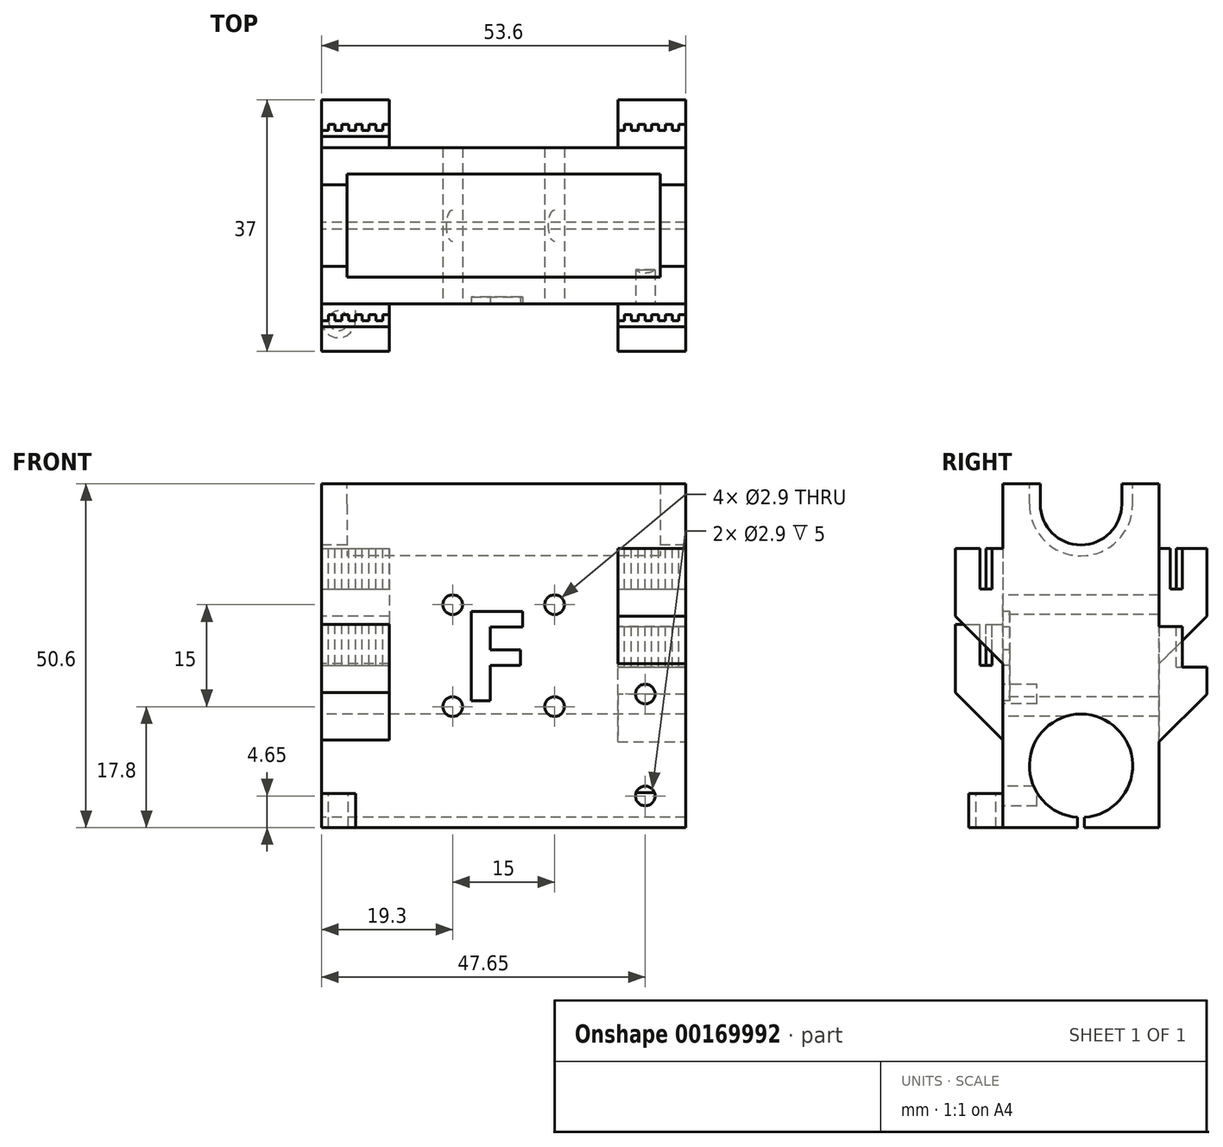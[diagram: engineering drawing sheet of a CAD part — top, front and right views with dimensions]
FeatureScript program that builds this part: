
annotation { "Feature Type Name" : "Feature", "Feature Type Description" : "" }
export const myFeature = defineFeature(function(context is Context, id is Id, definition is map)
    precondition{}
    {
        {
            assignVariable(context, id + "F0", {"name" : "LM8LUU", "anyValue" : 1.8});
        }
        {
            var Q0;
            Q0=qCreatedBy(makeId("Top.planeOp"),FACE);
            var sketch = newSketch(context, id + "F1", { "sketchPlane" : qUnion([Q0])});
            skLineSegment(sketch, "E0.bottom", {"start": v(0, 0) * mm, "end": v(53.6, 0) * mm});
            skLineSegment(sketch, "E0.top", {"start": v(0, 23) * mm, "end": v(53.6, 23) * mm});
            skLineSegment(sketch, "E0.left", {"start": v(0, 0) * mm, "end": v(0, 23) * mm});
            skLineSegment(sketch, "E0.right", {"start": v(53.6, 0) * mm, "end": v(53.6, 23) * mm});
            skSolve(sketch);
        }
        {
            var Q0;
            Q0=qSketchRegion(id+"F1",true);
            extrude(context, id + "F2", {"entities" : qUnion([Q0]), "depth" : 50.6 * mm});
        }
        {
            var Q0;
            Q0=makeQuery(id+"F2.opExtrude","SWEPT_FACE",FACE,{"disambiguationData":[OSD([sQuery(id+"F1.wireOp",EDGE,"E0.left")])]});
            var sketch = newSketch(context, id + "F3", { "sketchPlane" : qUnion([Q0])});
            skCircle(sketch, "E1", {"center": v(-11.5, 9.1) * mm, "radius": 7.6 * mm});
            skCircle(sketch, "E2", {"center": v(-11.5, 47.6) * mm, "radius": 6 * mm});
            skLineSegment(sketch, "E3", {"start": v(-23, 47.6) * mm, "end": v(0, 47.6) * mm, "construction": true});
            skLineSegment(sketch, "E4", {"start": v(-17.5, 50.6) * mm, "end": v(-17.5, 47.6) * mm});
            skLineSegment(sketch, "E5", {"start": v(-5.5, 50.6) * mm, "end": v(-5.5, 47.6) * mm});
            skLineSegment(sketch, "E6", {"start": v(-23, 9.1) * mm, "end": v(0, 9.1) * mm, "construction": true});
            skLineSegment(sketch, "E7", {"start": v(-11.5, 9.1) * mm, "end": v(-11.5, 0) * mm, "construction": true});
            skLineSegment(sketch, "E8", {"start": v(-11.5, 0) * mm, "end": v(-12, 0) * mm});
            skLineSegment(sketch, "E9", {"start": v(-12, 0) * mm, "end": v(-12, 1.52) * mm});
            skLineSegment(sketch, "E10", {"start": v(-12, 1.52) * mm, "end": v(-11, 1.52) * mm});
            skLineSegment(sketch, "E11", {"start": v(-11, 1.52) * mm, "end": v(-11, 0) * mm});
            skLineSegment(sketch, "E12", {"start": v(-11, 0) * mm, "end": v(-11.5, 0) * mm});
            skCircle(sketch, "E13", {"center": v(-11.5, 47.6) * mm, "radius": 7.6 * mm});
            skLineSegment(sketch, "E14", {"start": v(-3.9, 47.6) * mm, "end": v(-3.9, 50.6) * mm});
            skLineSegment(sketch, "E15", {"start": v(-19.1, 47.6) * mm, "end": v(-19.1, 50.6) * mm});
            skSolve(sketch);
        }
        {
            var Q0;
            {var subQ0=sQuery(id+"F3.wireOp",EDGE,"61a55092-bd36-442a-954f-b1d305e603b2");var subQ1=sQuery(id+"F3.wireOp",EDGE,"E1");var subQ3=makeQuery(id+"F3.imprint","INTERSECT",VERTEX,{"disambiguationData":[OD(0.0)],"derivedFrom":[subQ1,subQ0]});Q0=makeQuery(id+"F3.imprint","IMPRINT",FACE,{"disambiguationData":[TD([[makeQuery(id+"F3.imprint","IMPRINT",EDGE,{"disambiguationData":[TD([[subQ3,-1.0]])],"derivedFrom":subQ1}),1.0]])]});}
            var Q1;
            {var subQ0=sQuery(id+"F3.wireOp",EDGE,"ccdeb851-c584-4ba8-b480-4501c20c5f95");var subQ1=sQuery(id+"F3.wireOp",EDGE,"E1");var subQ3=makeQuery(id+"F3.imprint","INTERSECT",VERTEX,{"disambiguationData":[OD(0.0)],"derivedFrom":[subQ1,subQ0]});Q1=makeQuery(id+"F3.imprint","IMPRINT",FACE,{"disambiguationData":[TD([[makeQuery(id+"F3.imprint","IMPRINT",EDGE,{"disambiguationData":[TD([[subQ3,1.0]])],"derivedFrom":subQ1}),1.0]])]});}
            var Q2;
            Q2=makeQuery(id+"F3.imprint","IMPRINT",FACE,{"disambiguationData":[TD([[makeQuery(id+"F3.imprint","IMPRINT",EDGE,{"derivedFrom":sQuery(id+"F3.wireOp",EDGE,"E8")}),-1.0]])]});
            var Q3;
            {var subQ0=sQuery(id+"F3.wireOp",EDGE,"E10");Q3=makeQuery(id+"F3.imprint","IMPRINT",FACE,{"disambiguationData":[TD([[makeQuery(id+"F3.imprint","IMPRINT",EDGE,{"derivedFrom":subQ0}),-1.0]])]});}
            var Q4;
            {var subQ3=sQuery(id+"F3.wireOp",EDGE,"84843404-b723-4df1-a710-1511c094684b");Q4=makeQuery(id+"F3.imprint","IMPRINT",FACE,{"disambiguationData":[TD([[makeQuery(id+"F3.imprint","IMPRINT",EDGE,{"derivedFrom":subQ3}),-1.0]])]});}
            var Q5;
            {var subQ3=sQuery(id+"F3.wireOp",EDGE,"84843404-b723-4df1-a710-1511c094684b");Q5=makeQuery(id+"F3.imprint","IMPRINT",FACE,{"disambiguationData":[TD([[makeQuery(id+"F3.imprint","IMPRINT",EDGE,{"derivedFrom":subQ3}),1.0]])]});}
            var Q6;
            {var subQ7=sQuery(id+"F3.wireOp",EDGE,"E10");Q6=makeQuery(id+"F3.imprint","IMPRINT",FACE,{"disambiguationData":[TD([[makeQuery(id+"F3.imprint","IMPRINT",EDGE,{"derivedFrom":subQ7}),1.0]])]});}
            var Q7;
            {var subQ3=sQuery(id+"F3.wireOp",EDGE,"E5");Q7=makeQuery(id+"F3.imprint","IMPRINT",FACE,{"disambiguationData":[TD([[makeQuery(id+"F3.imprint","IMPRINT",EDGE,{"derivedFrom":subQ3}),-1.0]])]});}
            var Q8;
            {var subQ0=sQuery(id+"F3.wireOp",EDGE,"E4");Q8=makeQuery(id+"F3.imprint","IMPRINT",FACE,{"disambiguationData":[TD([[makeQuery(id+"F3.imprint","IMPRINT",EDGE,{"derivedFrom":subQ0}),1.0]])]});}
            var Q9;
            {var subQ0=sQuery(id+"F3.wireOp",EDGE,"E4");Q9=makeQuery(id+"F3.imprint","IMPRINT",FACE,{"disambiguationData":[TD([[makeQuery(id+"F3.imprint","IMPRINT",EDGE,{"derivedFrom":subQ0}),1.0]])]});}
            var Q10;
            {var subQ3=sQuery(id+"F3.wireOp",EDGE,"E5");Q10=makeQuery(id+"F3.imprint","IMPRINT",FACE,{"disambiguationData":[TD([[makeQuery(id+"F3.imprint","IMPRINT",EDGE,{"derivedFrom":subQ3}),-1.0]])]});}
            var Q11;
            {var subQ1=sQuery(id+"F3.wireOp",EDGE,"E2");var subQ4=makeQuery(id+"F3.imprint","INTERSECT",VERTEX,{"derivedFrom":[subQ1,sQuery(id+"F3.wireOp",EDGE,"E5")]});Q11=makeQuery(id+"F3.imprint","IMPRINT",FACE,{"disambiguationData":[TD([[makeQuery(id+"F3.imprint","IMPRINT",EDGE,{"disambiguationData":[TD([[subQ4,-1.0]])],"derivedFrom":subQ1}),1.0]])]});}
            extrude(context, id + "F4", {"entities" : qUnion([Q0, Q1, Q2, Q3, Q4, Q5, Q6, Q7, Q8, Q9, Q10, Q11]), "operationType" : NewBodyOperationType.REMOVE, "endBound" : BoundingType.THROUGH_ALL, "oppositeDirection" : true, "depth" : 25 * mm});
        }
        {
            var Q0;
            {var subQ3=sQuery(id+"F3.wireOp",EDGE,"E4");Q0=makeQuery(id+"F3.imprint","IMPRINT",FACE,{"disambiguationData":[TD([[makeQuery(id+"F3.imprint","IMPRINT",EDGE,{"derivedFrom":subQ3}),-1.0]])]});}
            var Q1;
            {var subQ3=sQuery(id+"F3.wireOp",EDGE,"E15");Q1=makeQuery(id+"F3.imprint","IMPRINT",FACE,{"disambiguationData":[TD([[makeQuery(id+"F3.imprint","IMPRINT",EDGE,{"derivedFrom":subQ3}),-1.0]])]});}
            var Q2;
            {var subQ3=sQuery(id+"F3.wireOp",EDGE,"E14");Q2=makeQuery(id+"F3.imprint","IMPRINT",FACE,{"disambiguationData":[TD([[makeQuery(id+"F3.imprint","IMPRINT",EDGE,{"derivedFrom":subQ3}),1.0]])]});}
            extrude(context, id + "F5", {"entities" : qUnion([Q0, Q1, Q2]), "operationType" : NewBodyOperationType.REMOVE, "oppositeDirection" : true, "depth" : (46.25 + getVariable(context, 'LM8LUU') * 2) * mm});
        }
        {
            var Q0;
            {var subQ3=sQuery(id+"F3.wireOp",EDGE,"E4");Q0=makeQuery(id+"F3.imprint","IMPRINT",FACE,{"disambiguationData":[TD([[makeQuery(id+"F3.imprint","IMPRINT",EDGE,{"derivedFrom":subQ3}),-1.0]])]});}
            var Q1;
            {var subQ3=sQuery(id+"F3.wireOp",EDGE,"E15");Q1=makeQuery(id+"F3.imprint","IMPRINT",FACE,{"disambiguationData":[TD([[makeQuery(id+"F3.imprint","IMPRINT",EDGE,{"derivedFrom":subQ3}),-1.0]])]});}
            var Q2;
            {var subQ3=sQuery(id+"F3.wireOp",EDGE,"E14");Q2=makeQuery(id+"F3.imprint","IMPRINT",FACE,{"disambiguationData":[TD([[makeQuery(id+"F3.imprint","IMPRINT",EDGE,{"derivedFrom":subQ3}),1.0]])]});}
            extrude(context, id + "F6", {"entities" : qUnion([Q0, Q1, Q2]), "operationType" : NewBodyOperationType.ADD, "oppositeDirection" : true, "depth" : (26.75 - getVariable(context, 'LM8LUU')) * mm});
        }
        {
            var Q0;
            {var subQ3=sQuery(id+"F3.wireOp",EDGE,"E4");Q0=makeQuery(id+"F3.imprint","IMPRINT",FACE,{"disambiguationData":[TD([[makeQuery(id+"F3.imprint","IMPRINT",EDGE,{"derivedFrom":subQ3}),-1.0]])]});}
            var Q1;
            {var subQ3=sQuery(id+"F3.wireOp",EDGE,"E15");Q1=makeQuery(id+"F3.imprint","IMPRINT",FACE,{"disambiguationData":[TD([[makeQuery(id+"F3.imprint","IMPRINT",EDGE,{"derivedFrom":subQ3}),-1.0]])]});}
            var Q2;
            {var subQ3=sQuery(id+"F3.wireOp",EDGE,"E14");Q2=makeQuery(id+"F3.imprint","IMPRINT",FACE,{"disambiguationData":[TD([[makeQuery(id+"F3.imprint","IMPRINT",EDGE,{"derivedFrom":subQ3}),1.0]])]});}
            extrude(context, id + "F7", {"entities" : qUnion([Q0, Q1, Q2]), "operationType" : NewBodyOperationType.REMOVE, "oppositeDirection" : true, "depth" : (23.25 + getVariable(context, 'LM8LUU')) * mm});
        }
        {
            var Q0;
            {var subQ3=sQuery(id+"F3.wireOp",EDGE,"E4");Q0=makeQuery(id+"F3.imprint","IMPRINT",FACE,{"disambiguationData":[TD([[makeQuery(id+"F3.imprint","IMPRINT",EDGE,{"derivedFrom":subQ3}),-1.0]])]});}
            var Q1;
            {var subQ3=sQuery(id+"F3.wireOp",EDGE,"E15");Q1=makeQuery(id+"F3.imprint","IMPRINT",FACE,{"disambiguationData":[TD([[makeQuery(id+"F3.imprint","IMPRINT",EDGE,{"derivedFrom":subQ3}),-1.0]])]});}
            var Q2;
            {var subQ3=sQuery(id+"F3.wireOp",EDGE,"E14");Q2=makeQuery(id+"F3.imprint","IMPRINT",FACE,{"disambiguationData":[TD([[makeQuery(id+"F3.imprint","IMPRINT",EDGE,{"derivedFrom":subQ3}),1.0]])]});}
            extrude(context, id + "F8", {"entities" : qUnion([Q0, Q1, Q2]), "operationType" : NewBodyOperationType.ADD, "oppositeDirection" : true, "depth" : 3.75 * mm});
        }
        {
            var Q0;
            Q0=makeQuery(id+"F2.opExtrude","SWEPT_FACE",FACE,{"disambiguationData":[OSD([sQuery(id+"F1.wireOp",EDGE,"E0.bottom")])]});
            var sketch = newSketch(context, id + "F9", { "sketchPlane" : qUnion([Q0])});
            skLineSegment(sketch, "E16.bottom", {"start": v(0, 29.9) * mm, "end": v(10, 29.9) * mm});
            skLineSegment(sketch, "E16.top", {"start": v(0, 9.9) * mm, "end": v(10, 9.9) * mm});
            skLineSegment(sketch, "E16.left", {"start": v(0, 29.9) * mm, "end": v(0, 9.9) * mm});
            skLineSegment(sketch, "E16.right", {"start": v(10, 29.9) * mm, "end": v(10, 9.9) * mm});
            skLineSegment(sketch, "E17.bottom", {"start": v(53.6, 41.1) * mm, "end": v(43.6, 41.1) * mm});
            skLineSegment(sketch, "E17.top", {"start": v(53.6, 21.1) * mm, "end": v(43.6, 21.1) * mm});
            skLineSegment(sketch, "E17.left", {"start": v(53.6, 41.1) * mm, "end": v(53.6, 21.1) * mm});
            skLineSegment(sketch, "E17.right", {"start": v(43.6, 41.1) * mm, "end": v(43.6, 21.1) * mm});
            skPoint(sketch, "E18", {"position": v(0, 47.6) * mm});
            skPoint(sketch, "E19", {"position": v(0, 9.4) * mm});
            skSolve(sketch);
        }
        {
            var Q0;
            Q0=qSketchRegion(id+"F9",true);
            extrude(context, id + "F10", {"entities" : qUnion([Q0]), "operationType" : NewBodyOperationType.ADD, "depth" : 7 * mm});
        }
        {
            var Q0;
            Q0=makeQuery(id+"F10.opExtrude","CAP_EDGE",EDGE,{"disambiguationData":[OSD([sQuery(id+"F9.wireOp",EDGE,"E16.top")])],"isStart":false});
            var Q1;
            Q1=makeQuery(id+"F10.opExtrude","CAP_EDGE",EDGE,{"disambiguationData":[OSD([sQuery(id+"F9.wireOp",EDGE,"E17.top")])],"isStart":false});
            chamfer(context, id + "F11", {"entities" : qUnion([Q0, Q1]), "width" : 10 * mm, "tangentPropagation" : true});
        }
        {
            var Q0;
            Q0=makeQuery(id+"F10.opExtrude","SWEPT_FACE",FACE,{"disambiguationData":[OSD([sQuery(id+"F9.wireOp",EDGE,"E16.bottom")])]});
            var sketch = newSketch(context, id + "F12", { "sketchPlane" : qUnion([Q0])});
            skLineSegment(sketch, "E20", {"start": v(-935.9, 0) * mm, "end": v(-935.88, -4.54) * mm});
            skLineSegment(sketch, "E21.left", {"start": v(0, -3.4) * mm, "end": v(0, -1.6) * mm});
            skLineSegment(sketch, "E22", {"start": v(6, -2.5) * mm, "end": v(7, -2.5) * mm});
            skLineSegment(sketch, "E23", {"start": v(4, -2.5) * mm, "end": v(5, -2.5) * mm});
            skLineSegment(sketch, "E24", {"start": v(0, -2.5) * mm, "end": v(1, -2.5) * mm});
            skLineSegment(sketch, "E25", {"start": v(7, -1.6) * mm, "end": v(8, -1.6) * mm});
            skLineSegment(sketch, "E26", {"start": v(2, -2.5) * mm, "end": v(3, -2.5) * mm});
            skLineSegment(sketch, "E27", {"start": v(3, -1.6) * mm, "end": v(4, -1.6) * mm});
            skLineSegment(sketch, "E28", {"start": v(8, -2.5) * mm, "end": v(9, -2.5) * mm});
            skLineSegment(sketch, "E29", {"start": v(8, -1.6) * mm, "end": v(8, -2.5) * mm});
            skLineSegment(sketch, "E30", {"start": v(9, -2.5) * mm, "end": v(9, -1.6) * mm});
            skLineSegment(sketch, "E31", {"start": v(10, -1.6) * mm, "end": v(10, -2.5) * mm});
            skLineSegment(sketch, "E32", {"start": v(6, -1.6) * mm, "end": v(6, -2.5) * mm});
            skLineSegment(sketch, "E33", {"start": v(2, -1.6) * mm, "end": v(2, -2.5) * mm});
            skLineSegment(sketch, "E34", {"start": v(1, -1.6) * mm, "end": v(2, -1.6) * mm});
            skLineSegment(sketch, "E35", {"start": v(1, -2.5) * mm, "end": v(1, -1.6) * mm});
            skLineSegment(sketch, "E36", {"start": v(9, -1.6) * mm, "end": v(10, -1.6) * mm});
            skLineSegment(sketch, "E37", {"start": v(5, -1.6) * mm, "end": v(6, -1.6) * mm});
            skLineSegment(sketch, "E38", {"start": v(5, -2.5) * mm, "end": v(5, -1.6) * mm});
            skLineSegment(sketch, "E39", {"start": v(3, -2.5) * mm, "end": v(3, -1.6) * mm});
            skLineSegment(sketch, "E40", {"start": v(4, -1.6) * mm, "end": v(4, -2.5) * mm});
            skLineSegment(sketch, "E41", {"start": v(7, -2.5) * mm, "end": v(7, -1.6) * mm});
            skLineSegment(sketch, "E42", {"start": v(0, -1.6) * mm, "end": v(0, -2.5) * mm});
            skLineSegment(sketch, "E43", {"start": v(10, -2.5) * mm, "end": v(10, -3.4) * mm});
            skLineSegment(sketch, "E44", {"start": v(0, -3.4) * mm, "end": v(10, -3.4) * mm});
            skLineSegment(sketch, "E45", {"start": v(5.3, -1.6) * mm, "end": v(5.3, 0) * mm});
            skSolve(sketch);
        }
        {
            var Q0;
            Q0=qSketchRegion(id+"F12",true);
            extrude(context, id + "F13", {"entities" : qUnion([Q0]), "operationType" : NewBodyOperationType.REMOVE, "oppositeDirection" : true, "depth" : 6 * mm});
        }
        {
            var Q0;
            Q0=makeQuery(id+"F10.opExtrude","SWEPT_FACE",FACE,{"disambiguationData":[OSD([sQuery(id+"F9.wireOp",EDGE,"E17.bottom")])]});
            var sketch = newSketch(context, id + "F14", { "sketchPlane" : qUnion([Q0])});
            skLineSegment(sketch, "E46.left", {"start": v(43.6, -3.4) * mm, "end": v(43.6, -1.6) * mm});
            skLineSegment(sketch, "E47", {"start": v(49.6, -2.5) * mm, "end": v(50.6, -2.5) * mm});
            skLineSegment(sketch, "E48", {"start": v(47.6, -2.5) * mm, "end": v(48.6, -2.5) * mm});
            skLineSegment(sketch, "E49", {"start": v(43.6, -2.5) * mm, "end": v(44.6, -2.5) * mm});
            skLineSegment(sketch, "E50", {"start": v(50.6, -1.6) * mm, "end": v(51.6, -1.6) * mm});
            skLineSegment(sketch, "E51", {"start": v(45.6, -2.5) * mm, "end": v(46.6, -2.5) * mm});
            skLineSegment(sketch, "E52", {"start": v(46.6, -1.6) * mm, "end": v(47.6, -1.6) * mm});
            skLineSegment(sketch, "E53", {"start": v(51.6, -2.5) * mm, "end": v(52.6, -2.5) * mm});
            skLineSegment(sketch, "E54", {"start": v(51.6, -1.6) * mm, "end": v(51.6, -2.5) * mm});
            skLineSegment(sketch, "E55", {"start": v(52.6, -2.5) * mm, "end": v(52.6, -1.6) * mm});
            skLineSegment(sketch, "E56", {"start": v(53.6, -1.6) * mm, "end": v(53.6, -2.5) * mm});
            skLineSegment(sketch, "E57", {"start": v(49.6, -1.6) * mm, "end": v(49.6, -2.5) * mm});
            skLineSegment(sketch, "E58", {"start": v(45.6, -1.6) * mm, "end": v(45.6, -2.5) * mm});
            skLineSegment(sketch, "E59", {"start": v(44.6, -1.6) * mm, "end": v(45.6, -1.6) * mm});
            skLineSegment(sketch, "E60", {"start": v(44.6, -2.5) * mm, "end": v(44.6, -1.6) * mm});
            skLineSegment(sketch, "E61", {"start": v(52.6, -1.6) * mm, "end": v(53.6, -1.6) * mm});
            skLineSegment(sketch, "E62", {"start": v(48.6, -1.6) * mm, "end": v(49.6, -1.6) * mm});
            skLineSegment(sketch, "E63", {"start": v(48.6, -2.5) * mm, "end": v(48.6, -1.6) * mm});
            skLineSegment(sketch, "E64", {"start": v(46.6, -2.5) * mm, "end": v(46.6, -1.6) * mm});
            skLineSegment(sketch, "E65", {"start": v(47.6, -1.6) * mm, "end": v(47.6, -2.5) * mm});
            skLineSegment(sketch, "E66", {"start": v(50.6, -2.5) * mm, "end": v(50.6, -1.6) * mm});
            skLineSegment(sketch, "E67", {"start": v(43.6, -1.6) * mm, "end": v(43.6, -2.5) * mm});
            skLineSegment(sketch, "E68", {"start": v(53.6, -2.5) * mm, "end": v(53.6, -3.4) * mm});
            skLineSegment(sketch, "E69", {"start": v(43.6, -3.4) * mm, "end": v(53.6, -3.4) * mm});
            skLineSegment(sketch, "E70", {"start": v(48.83, -1.6) * mm, "end": v(48.83, 0) * mm});
            skSolve(sketch);
        }
        {
            var Q0;
            Q0=qSketchRegion(id+"F14",true);
            extrude(context, id + "F15", {"entities" : qUnion([Q0]), "operationType" : NewBodyOperationType.REMOVE, "oppositeDirection" : true, "depth" : 6 * mm});
        }
        {
            var Q0;
            Q0=makeQuery(id+"F2.opExtrude","SWEPT_FACE",FACE,{"disambiguationData":[OSD([sQuery(id+"F1.wireOp",EDGE,"E0.top")])]});
            var sketch = newSketch(context, id + "F16", { "sketchPlane" : qUnion([Q0])});
            skLineSegment(sketch, "E71.bottom", {"start": v(-53.6, 9.6) * mm, "end": v(-43.6, 9.6) * mm});
            skLineSegment(sketch, "E71.top", {"start": v(-53.6, 29.6) * mm, "end": v(-43.6, 29.6) * mm});
            skLineSegment(sketch, "E71.left", {"start": v(-53.6, 9.6) * mm, "end": v(-53.6, 29.6) * mm});
            skLineSegment(sketch, "E71.right", {"start": v(-43.6, 9.6) * mm, "end": v(-43.6, 29.6) * mm});
            skLineSegment(sketch, "E72.bottom", {"start": v(0, 41.1) * mm, "end": v(-10, 41.1) * mm});
            skLineSegment(sketch, "E72.top", {"start": v(0, 21.1) * mm, "end": v(-10, 21.1) * mm});
            skLineSegment(sketch, "E72.left", {"start": v(0, 41.1) * mm, "end": v(0, 21.1) * mm});
            skLineSegment(sketch, "E72.right", {"start": v(-10, 41.1) * mm, "end": v(-10, 21.1) * mm});
            skSolve(sketch);
        }
        {
            var Q0;
            Q0=qSketchRegion(id+"F16",true);
            extrude(context, id + "F17", {"entities" : qUnion([Q0]), "operationType" : NewBodyOperationType.ADD, "depth" : 7 * mm});
        }
        {
            var Q0;
            Q0=makeQuery(id+"F17.opExtrude","SWEPT_FACE",FACE,{"disambiguationData":[OSD([sQuery(id+"F16.wireOp",EDGE,"E71.top")])]});
            var sketch = newSketch(context, id + "F18", { "sketchPlane" : qUnion([Q0])});
            skLineSegment(sketch, "E73.left", {"start": v(43.6, 24.6) * mm, "end": v(43.6, 26.4) * mm});
            skLineSegment(sketch, "E74", {"start": v(49.6, 25.5) * mm, "end": v(50.6, 25.5) * mm});
            skLineSegment(sketch, "E75", {"start": v(47.6, 25.5) * mm, "end": v(48.6, 25.5) * mm});
            skLineSegment(sketch, "E76", {"start": v(43.6, 25.5) * mm, "end": v(44.6, 25.5) * mm});
            skLineSegment(sketch, "E77", {"start": v(50.6, 26.4) * mm, "end": v(51.6, 26.4) * mm});
            skLineSegment(sketch, "E78", {"start": v(45.6, 25.5) * mm, "end": v(46.6, 25.5) * mm});
            skLineSegment(sketch, "E79", {"start": v(46.6, 26.4) * mm, "end": v(47.6, 26.4) * mm});
            skLineSegment(sketch, "E80", {"start": v(51.6, 25.5) * mm, "end": v(52.6, 25.5) * mm});
            skLineSegment(sketch, "E81", {"start": v(51.6, 26.4) * mm, "end": v(51.6, 25.5) * mm});
            skLineSegment(sketch, "E82", {"start": v(52.6, 25.5) * mm, "end": v(52.6, 26.4) * mm});
            skLineSegment(sketch, "E83", {"start": v(53.6, 26.4) * mm, "end": v(53.6, 25.5) * mm});
            skLineSegment(sketch, "E84", {"start": v(49.6, 26.4) * mm, "end": v(49.6, 25.5) * mm});
            skLineSegment(sketch, "E85", {"start": v(45.6, 26.4) * mm, "end": v(45.6, 25.5) * mm});
            skLineSegment(sketch, "E86", {"start": v(44.6, 26.4) * mm, "end": v(45.6, 26.4) * mm});
            skLineSegment(sketch, "E87", {"start": v(44.6, 25.5) * mm, "end": v(44.6, 26.4) * mm});
            skLineSegment(sketch, "E88", {"start": v(52.6, 26.4) * mm, "end": v(53.6, 26.4) * mm});
            skLineSegment(sketch, "E89", {"start": v(48.6, 26.4) * mm, "end": v(49.6, 26.4) * mm});
            skLineSegment(sketch, "E90", {"start": v(48.6, 25.5) * mm, "end": v(48.6, 26.4) * mm});
            skLineSegment(sketch, "E91", {"start": v(46.6, 25.5) * mm, "end": v(46.6, 26.4) * mm});
            skLineSegment(sketch, "E92", {"start": v(47.6, 26.4) * mm, "end": v(47.6, 25.5) * mm});
            skLineSegment(sketch, "E93", {"start": v(50.6, 25.5) * mm, "end": v(50.6, 26.4) * mm});
            skLineSegment(sketch, "E94", {"start": v(43.6, 26.4) * mm, "end": v(43.6, 25.5) * mm});
            skLineSegment(sketch, "E95", {"start": v(53.6, 25.5) * mm, "end": v(53.6, 24.6) * mm});
            skLineSegment(sketch, "E96", {"start": v(43.6, 24.6) * mm, "end": v(53.6, 24.6) * mm});
            skLineSegment(sketch, "E97", {"start": v(48.6, 24.6) * mm, "end": v(48.6, 23) * mm});
            skSolve(sketch);
        }
        {
            var Q0;
            {var subQ4=sQuery(id+"F18.wireOp",EDGE,"E73.left");Q0=makeQuery(id+"F18.imprint","IMPRINT",FACE,{"disambiguationData":[TD([[makeQuery(id+"F18.imprint","IMPRINT",EDGE,{"derivedFrom":subQ4}),1.0]])]});}
            extrude(context, id + "F19", {"entities" : qUnion([Q0]), "operationType" : NewBodyOperationType.REMOVE, "oppositeDirection" : true, "depth" : 6 * mm});
        }
        {
            var Q0;
            Q0=makeQuery(id+"F17.opExtrude","SWEPT_FACE",FACE,{"disambiguationData":[OSD([sQuery(id+"F16.wireOp",EDGE,"E72.bottom")])]});
            var sketch = newSketch(context, id + "F20", { "sketchPlane" : qUnion([Q0])});
            skLineSegment(sketch, "E98", {"start": v(6, 25.5) * mm, "end": v(7, 25.5) * mm});
            skLineSegment(sketch, "E99", {"start": v(4, 25.5) * mm, "end": v(5, 25.5) * mm});
            skLineSegment(sketch, "E100", {"start": v(0, 25.5) * mm, "end": v(1, 25.5) * mm});
            skLineSegment(sketch, "E101", {"start": v(7, 26.4) * mm, "end": v(8, 26.4) * mm});
            skLineSegment(sketch, "E102", {"start": v(2, 25.5) * mm, "end": v(3, 25.5) * mm});
            skLineSegment(sketch, "E103", {"start": v(3, 26.4) * mm, "end": v(4, 26.4) * mm});
            skLineSegment(sketch, "E104", {"start": v(8, 25.5) * mm, "end": v(9, 25.5) * mm});
            skLineSegment(sketch, "E105", {"start": v(8, 26.4) * mm, "end": v(8, 25.5) * mm});
            skLineSegment(sketch, "E106", {"start": v(9, 25.5) * mm, "end": v(9, 26.4) * mm});
            skLineSegment(sketch, "E107", {"start": v(10, 26.4) * mm, "end": v(10, 25.5) * mm});
            skLineSegment(sketch, "E108", {"start": v(6, 26.4) * mm, "end": v(6, 25.5) * mm});
            skLineSegment(sketch, "E109", {"start": v(2, 26.4) * mm, "end": v(2, 25.5) * mm});
            skLineSegment(sketch, "E110", {"start": v(1, 26.4) * mm, "end": v(2, 26.4) * mm});
            skLineSegment(sketch, "E111", {"start": v(1, 25.5) * mm, "end": v(1, 26.4) * mm});
            skLineSegment(sketch, "E112", {"start": v(9, 26.4) * mm, "end": v(10, 26.4) * mm});
            skLineSegment(sketch, "E113", {"start": v(5, 26.4) * mm, "end": v(6, 26.4) * mm});
            skLineSegment(sketch, "E114", {"start": v(5, 25.5) * mm, "end": v(5, 26.4) * mm});
            skLineSegment(sketch, "E115", {"start": v(3, 25.5) * mm, "end": v(3, 26.4) * mm});
            skLineSegment(sketch, "E116", {"start": v(4, 26.4) * mm, "end": v(4, 25.5) * mm});
            skLineSegment(sketch, "E117", {"start": v(7, 25.5) * mm, "end": v(7, 26.4) * mm});
            skLineSegment(sketch, "E118", {"start": v(10, 25.5) * mm, "end": v(10, 24.6) * mm});
            skLineSegment(sketch, "E119", {"start": v(0, 24.6) * mm, "end": v(10, 24.6) * mm});
            skLineSegment(sketch, "E120", {"start": v(5, 24.6) * mm, "end": v(5, 23) * mm});
            skLineSegment(sketch, "E121", {"start": v(0, 24.6) * mm, "end": v(0, 25.5) * mm});
            skSolve(sketch);
        }
        {
            var Q0;
            Q0=makeQuery(id+"F20.imprint","IMPRINT",FACE,{"disambiguationData":[TD([[makeQuery(id+"F20.imprint","IMPRINT",EDGE,{"derivedFrom":sQuery(id+"F20.wireOp",EDGE,"E98")}),-1.0]])]});
            extrude(context, id + "F21", {"entities" : qUnion([Q0]), "operationType" : NewBodyOperationType.REMOVE, "oppositeDirection" : true, "depth" : 6 * mm});
        }
        {
            var Q0;
            Q0=makeQuery(id+"F17.opExtrude","CAP_EDGE",EDGE,{"disambiguationData":[OSD([sQuery(id+"F16.wireOp",EDGE,"E72.top")])],"isStart":false});
            var Q1;
            Q1=makeQuery(id+"F17.opExtrude","CAP_EDGE",EDGE,{"disambiguationData":[OSD([sQuery(id+"F16.wireOp",EDGE,"E71.bottom")])],"isStart":false});
            chamfer(context, id + "F22", {"entities" : qUnion([Q0, Q1]), "width" : 10 * mm, "tangentPropagation" : true});
        }
        {
            var Q0;
            Q0=makeQuery(id+"F2.opExtrude","SWEPT_FACE",FACE,{"disambiguationData":[OSD([sQuery(id+"F1.wireOp",EDGE,"E0.bottom")])]});
            var sketch = newSketch(context, id + "F23", { "sketchPlane" : qUnion([Q0])});
            skCircle(sketch, "E122", {"center": v(19.3, 32.8) * mm, "radius": 1.45 * mm});
            skCircle(sketch, "E123", {"center": v(34.3, 32.8) * mm, "radius": 1.45 * mm});
            skCircle(sketch, "E124", {"center": v(19.3, 17.8) * mm, "radius": 1.45 * mm});
            skCircle(sketch, "E125", {"center": v(34.3, 17.8) * mm, "radius": 1.45 * mm});
            skLineSegment(sketch, "E126", {"start": v(19.3, 32.8) * mm, "end": v(0, 32.8) * mm});
            skLineSegment(sketch, "E127", {"start": v(34.3, 17.8) * mm, "end": v(53.6, 17.8) * mm});
            skLineSegment(sketch, "E128", {"start": v(34.3, 32.8) * mm, "end": v(34.3, 50.6) * mm});
            skLineSegment(sketch, "E129", {"start": v(19.3, 17.8) * mm, "end": v(19.3, 0) * mm});
            skCircle(sketch, "E130", {"center": v(26.8, 3.68) * mm, "radius": 1.68 * mm});
            skLineSegment(sketch, "E131", {"start": v(26.8, 0) * mm, "end": v(26.8, 13.82) * mm, "construction": true});
            skSolve(sketch);
        }
        {
            var Q0;
            Q0=makeQuery(id+"F23.imprint","IMPRINT",FACE,{"disambiguationData":[TD([[makeQuery(id+"F23.imprint","IMPRINT",EDGE,{"derivedFrom":sQuery(id+"F23.wireOp",EDGE,"E122")}),1.0]])]});
            var Q1;
            Q1=makeQuery(id+"F23.imprint","IMPRINT",FACE,{"disambiguationData":[TD([[makeQuery(id+"F23.imprint","IMPRINT",EDGE,{"derivedFrom":sQuery(id+"F23.wireOp",EDGE,"E123")}),1.0]])]});
            var Q2;
            Q2=makeQuery(id+"F23.imprint","IMPRINT",FACE,{"disambiguationData":[TD([[makeQuery(id+"F23.imprint","IMPRINT",EDGE,{"derivedFrom":sQuery(id+"F23.wireOp",EDGE,"E124")}),1.0]])]});
            var Q3;
            Q3=makeQuery(id+"F23.imprint","IMPRINT",FACE,{"disambiguationData":[TD([[makeQuery(id+"F23.imprint","IMPRINT",EDGE,{"derivedFrom":sQuery(id+"F23.wireOp",EDGE,"E125")}),1.0]])]});
            var Q4;
            Q4=makeQuery(id+"F23.imprint","IMPRINT",FACE,{"disambiguationData":[TD([[makeQuery(id+"F23.imprint","IMPRINT",EDGE,{"derivedFrom":sQuery(id+"F23.wireOp",EDGE,"E122")}),1.0]])]});
            var Q5;
            Q5=makeQuery(id+"F23.imprint","IMPRINT",FACE,{"disambiguationData":[TD([[makeQuery(id+"F23.imprint","IMPRINT",EDGE,{"derivedFrom":sQuery(id+"F23.wireOp",EDGE,"E123")}),1.0]])]});
            var Q6;
            Q6=makeQuery(id+"F23.imprint","IMPRINT",FACE,{"disambiguationData":[TD([[makeQuery(id+"F23.imprint","IMPRINT",EDGE,{"derivedFrom":sQuery(id+"F23.wireOp",EDGE,"E125")}),1.0]])]});
            var Q7;
            Q7=makeQuery(id+"F23.imprint","IMPRINT",FACE,{"disambiguationData":[TD([[makeQuery(id+"F23.imprint","IMPRINT",EDGE,{"derivedFrom":sQuery(id+"F23.wireOp",EDGE,"E124")}),1.0]])]});
            extrude(context, id + "F24", {"entities" : qUnion([Q0, Q1, Q2, Q3, Q4, Q5, Q6, Q7]), "operationType" : NewBodyOperationType.REMOVE, "endBound" : BoundingType.THROUGH_ALL, "oppositeDirection" : true, "depth" : 25 * mm});
        }
        {
            var Q0;
            Q0=makeQuery(id+"F2.opExtrude","SWEPT_FACE",FACE,{"disambiguationData":[OSD([sQuery(id+"F1.wireOp",EDGE,"E0.bottom")])]});
            var sketch = newSketch(context, id + "F25", { "sketchPlane" : qUnion([Q0])});
            skCircle(sketch, "E132", {"center": v(47.65, 19.65) * mm, "radius": 1.45 * mm});
            skCircle(sketch, "E133", {"center": v(47.65, 4.65) * mm, "radius": 1.45 * mm});
            skSolve(sketch);
        }
        {
            var Q0;
            Q0=qSketchRegion(id+"F25",true);
            extrude(context, id + "F26", {"entities" : qUnion([Q0]), "operationType" : NewBodyOperationType.REMOVE, "oppositeDirection" : true, "depth" : 5 * mm});
        }
        {
            var Q0;
            Q0=makeQuery(id+"F2.opExtrude","SWEPT_FACE",FACE,{"disambiguationData":[OSD([sQuery(id+"F1.wireOp",EDGE,"E0.bottom")])]});
            var sketch = newSketch(context, id + "F27", { "sketchPlane" : qUnion([Q0])});
            skText(sketch, "E134", { "text": "F", "fontName": "OpenSans-Bold.ttf"});
            skLineSegment(sketch, "E135", {"start": v(19.3, 32.8) * mm, "end": v(19.3, 17.8) * mm, "construction": true});
            skLineSegment(sketch, "E136", {"start": v(19.3, 17.8) * mm, "end": v(34.3, 17.8) * mm, "construction": true});
            skLineSegment(sketch, "E137", {"start": v(34.3, 17.8) * mm, "end": v(34.3, 32.8) * mm, "construction": true});
            skLineSegment(sketch, "E138", {"start": v(34.3, 32.8) * mm, "end": v(19.3, 32.8) * mm, "construction": true});
            skLineSegment(sketch, "E139", {"start": v(19.3, 25.3) * mm, "end": v(22.2, 25.3) * mm, "construction": true});
            skLineSegment(sketch, "E140", {"start": v(31.4, 25.3) * mm, "end": v(34.3, 25.3) * mm, "construction": true});
            skLineSegment(sketch, "E141", {"start": v(26.8, 18.66) * mm, "end": v(26.8, 17.8) * mm, "construction": true});
            skLineSegment(sketch, "E142", {"start": v(26.8, 32.8) * mm, "end": v(26.8, 31.94) * mm, "construction": true});
            const initialGuessF27  = {"E134": [0.0204, 0.01866, 1, 0, 0.01328]};
            skSetInitialGuess(sketch, initialGuessF27);
            skSolve(sketch);
        }
        {
            var Q0;
            Q0=qSketchRegion(id+"F27",true);
            extrude(context, id + "F28", {"entities" : qUnion([Q0]), "operationType" : NewBodyOperationType.REMOVE, "oppositeDirection" : true, "depth" : 1 * mm});
        }
        {
            var Q0;
            Q0=makeQuery(id+"F2.opExtrude","SWEPT_FACE",FACE,{"disambiguationData":[OSD([sQuery(id+"F1.wireOp",EDGE,"E0.bottom")])]});
            var sketch = newSketch(context, id + "F29", { "sketchPlane" : qUnion([Q0])});
            skLineSegment(sketch, "E143.bottom", {"start": v(0, 0) * mm, "end": v(5, 0) * mm});
            skLineSegment(sketch, "E143.top", {"start": v(0, 5) * mm, "end": v(5, 5) * mm});
            skLineSegment(sketch, "E143.left", {"start": v(0, 0) * mm, "end": v(0, 5) * mm});
            skLineSegment(sketch, "E143.right", {"start": v(5, 0) * mm, "end": v(5, 5) * mm});
            skSolve(sketch);
        }
        {
            var Q0;
            Q0=qSketchRegion(id+"F29",true);
            var Q1;
            Q1 = qSketchRegion(id + "F31", true);
            extrude(context, id + "F30", {"entities" : qUnion([Q0, Q1]), "operationType" : NewBodyOperationType.ADD, "depth" : 5 * mm});
        }
        {
            var Q0;
            Q0=makeQuery(id+"F30.opExtrude","SWEPT_FACE",FACE,{"disambiguationData":[OSD([sQuery(id+"F29.wireOp",EDGE,"E143.top")])]});
            var sketch = newSketch(context, id + "F31", { "sketchPlane" : qUnion([Q0])});
            skCircle(sketch, "E144", {"center": v(2.5, -2.5) * mm, "radius": 1.45 * mm});
            skSolve(sketch);
        }
        {
            var Q0;
            Q0=qSketchRegion(id+"F31",true);
            extrude(context, id + "F32", {"entities" : qUnion([Q0]), "operationType" : NewBodyOperationType.REMOVE, "oppositeDirection" : true, "depth" : 25 * mm});
        }
        {
            var Q0;
            Q0=makeQuery(id+"F30.opExtrude","CAP_EDGE",EDGE,{"disambiguationData":[OSD([sQuery(id+"F29.wireOp",EDGE,"E143.left")])],"isStart":false});
            var Q1;
            Q1=makeQuery(id+"F30.opExtrude","CAP_EDGE",EDGE,{"disambiguationData":[OSD([sQuery(id+"F29.wireOp",EDGE,"E143.right")])],"isStart":false});
            fillet(context, id + "F33", {"entities" : qUnion([Q0, Q1]), "radius" : 2.5 * mm, "tangentPropagation" : true, "allowEdgeOverflow" : false});
        }
    });
